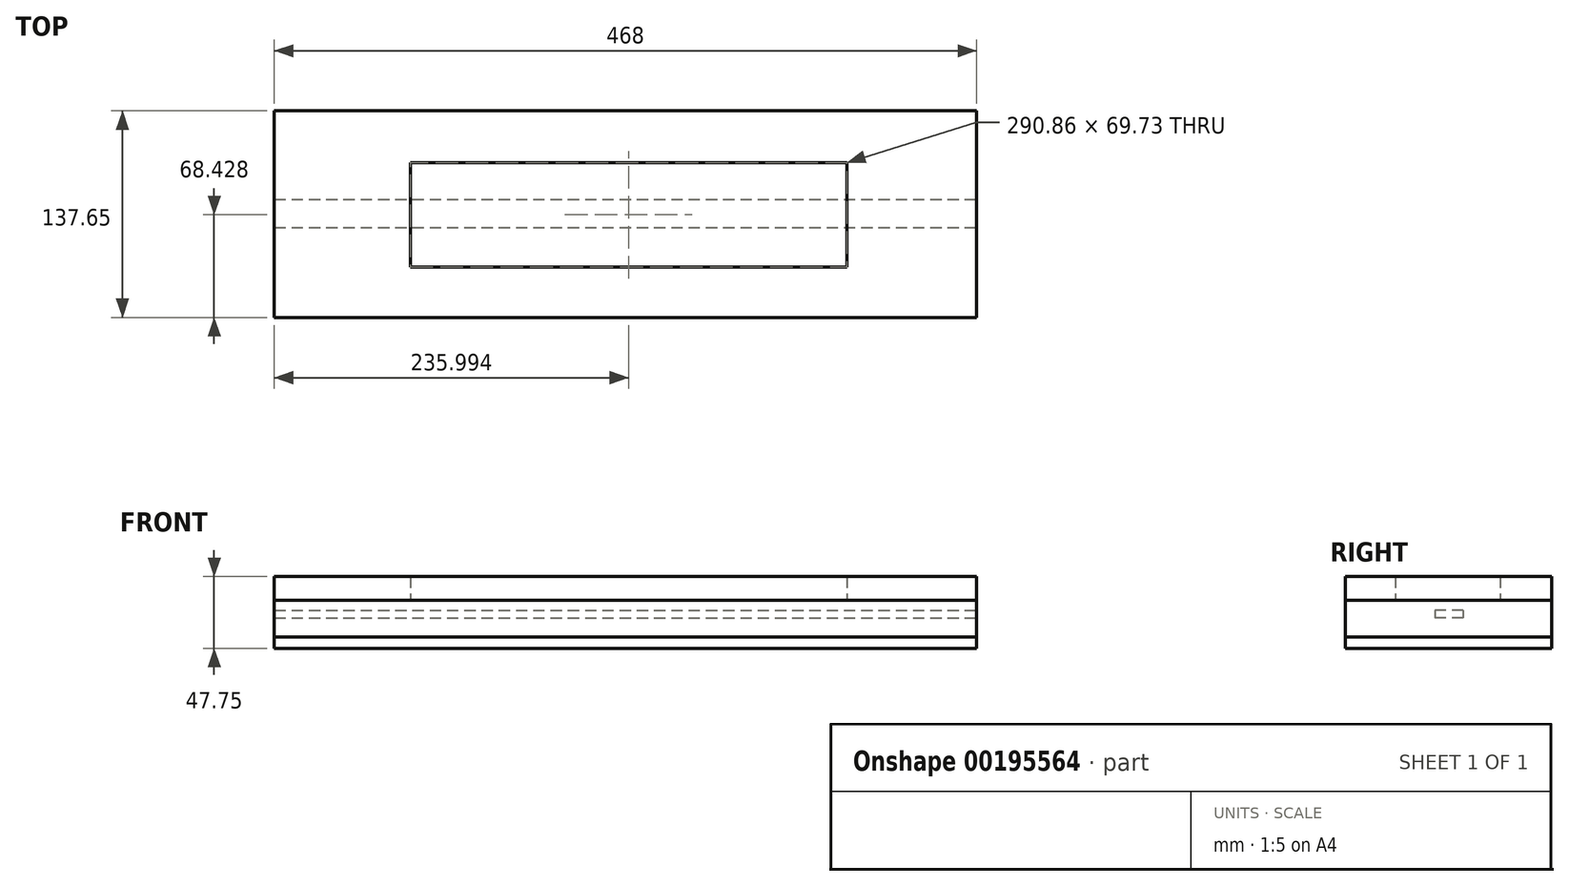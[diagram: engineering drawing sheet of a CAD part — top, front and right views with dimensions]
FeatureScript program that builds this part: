
annotation { "Feature Type Name" : "Feature", "Feature Type Description" : "" }
export const myFeature = defineFeature(function(context is Context, id is Id, definition is map)
    precondition{}
    {
        {
            var Q0;
            Q0=qCreatedBy(makeId("Top.planeOp"),FACE);
            var sketch = newSketch(context, id + "F0", { "sketchPlane" : qUnion([Q0])});
            skLineSegment(sketch, "E0.bottom", {"start": v(-202.47, -68.03) * mm, "end": v(265.53, -68.03) * mm});
            skLineSegment(sketch, "E0.top", {"start": v(-202.47, 69.62) * mm, "end": v(265.53, 69.62) * mm});
            skLineSegment(sketch, "E0.left", {"start": v(-202.47, -68.03) * mm, "end": v(-202.47, 69.62) * mm});
            skLineSegment(sketch, "E0.right", {"start": v(265.53, -68.03) * mm, "end": v(265.53, 69.62) * mm});
            skSolve(sketch);
        }
        {
            var Q0;
            Q0=qSketchRegion(id+"F0",true);
            extrude(context, id + "F1", {"entities" : qUnion([Q0]), "depth" : 7.37 * mm});
        }
        {
            var Q0;
            Q0=makeQuery(id+"F1.opExtrude","CAP_FACE",FACE,{"disambiguationData":[OSD([sQuery(id+"F0.wireOp",EDGE,"E0.bottom"),sQuery(id+"F0.wireOp",EDGE,"E0.top"),sQuery(id+"F0.wireOp",EDGE,"E0.left"),sQuery(id+"F0.wireOp",EDGE,"E0.right")])],"isStart":false});
            cPlane(context, id + "F2", {"entities" : qUnion([Q0]), "cplaneType" : CPlaneType.OFFSET, "offset" : 12.7 * mm, "width" : 152.4 * mm, "height" : 152.4 * mm});
        }
        {
            var Q0;
            Q0=qCreatedBy(id+"F2.planeOp",FACE);
            var sketch = newSketch(context, id + "F3", { "sketchPlane" : qUnion([Q0])});
            skLineSegment(sketch, "E1.bottom", {"start": v(-202.44, 10.56) * mm, "end": v(265.41, 10.56) * mm});
            skLineSegment(sketch, "E1.top", {"start": v(-202.44, -8.17) * mm, "end": v(265.41, -8.17) * mm});
            skLineSegment(sketch, "E1.left", {"start": v(-202.44, 10.56) * mm, "end": v(-202.44, -8.17) * mm});
            skLineSegment(sketch, "E1.right", {"start": v(265.41, 10.56) * mm, "end": v(265.41, -8.17) * mm});
            skSolve(sketch);
        }
        {
            var Q0;
            Q0 = qSketchRegion(id + "F3", true);
            extrude(context, id + "F4", {"entities" : qUnion([Q0]), "depth" : 5.08 * mm});
        }
        {
            var Q0;
            Q0=makeQuery(id+"F1.opExtrude","CAP_FACE",FACE,{"disambiguationData":[OSD([sQuery(id+"F0.wireOp",EDGE,"E0.bottom"),sQuery(id+"F0.wireOp",EDGE,"E0.top"),sQuery(id+"F0.wireOp",EDGE,"E0.left"),sQuery(id+"F0.wireOp",EDGE,"E0.right")])],"isStart":false});
            var sketch = newSketch(context, id + "F5", { "sketchPlane" : qUnion([Q0])});
            skLineSegment(sketch, "E2.bottom", {"start": v(-202.47, 69.62) * mm, "end": v(265.53, 69.62) * mm});
            skLineSegment(sketch, "E2.top", {"start": v(-202.47, -68.03) * mm, "end": v(265.53, -68.03) * mm});
            skLineSegment(sketch, "E2.left", {"start": v(-202.47, 69.62) * mm, "end": v(-202.47, -68.03) * mm});
            skLineSegment(sketch, "E2.right", {"start": v(265.53, 69.62) * mm, "end": v(265.53, -68.03) * mm});
            skSolve(sketch);
        }
        {
            var Q0;
            Q0 = qSketchRegion(id + "F5", true);
            extrude(context, id + "F6", {"entities" : qUnion([Q0]), "depth" : 24.64 * mm});
        }
        {
            var Q0;
            Q0=makeQuery(id+"F6.opExtrude","CAP_FACE",FACE,{"disambiguationData":[OSD([sQuery(id+"F5.wireOp",EDGE,"E2.bottom"),sQuery(id+"F5.wireOp",EDGE,"E2.top"),sQuery(id+"F5.wireOp",EDGE,"E2.left"),sQuery(id+"F5.wireOp",EDGE,"E2.right")])],"isStart":false});
            var sketch = newSketch(context, id + "F7", { "sketchPlane" : qUnion([Q0])});
            skLineSegment(sketch, "E3.bottom", {"start": v(-202.47, 69.62) * mm, "end": v(265.53, 69.62) * mm});
            skLineSegment(sketch, "E3.top", {"start": v(-202.47, -68.03) * mm, "end": v(265.53, -68.03) * mm});
            skLineSegment(sketch, "E3.left", {"start": v(-202.47, 69.62) * mm, "end": v(-202.47, -68.03) * mm});
            skLineSegment(sketch, "E3.right", {"start": v(265.53, 69.62) * mm, "end": v(265.53, -68.03) * mm});
            skLineSegment(sketch, "E4.bottom", {"start": v(-111.9, 35.26) * mm, "end": v(178.95, 35.26) * mm});
            skLineSegment(sketch, "E4.top", {"start": v(-111.9, -34.46) * mm, "end": v(178.95, -34.46) * mm});
            skLineSegment(sketch, "E4.left", {"start": v(-111.9, 35.26) * mm, "end": v(-111.9, -34.46) * mm});
            skLineSegment(sketch, "E4.right", {"start": v(178.95, 35.26) * mm, "end": v(178.95, -34.46) * mm});
            skSolve(sketch);
        }
        {
            var Q0;
            Q0 = qSketchRegion(id + "F7", true);
            extrude(context, id + "F8", {"entities" : qUnion([Q0]), "depth" : 15.75 * mm});
        }
    });
